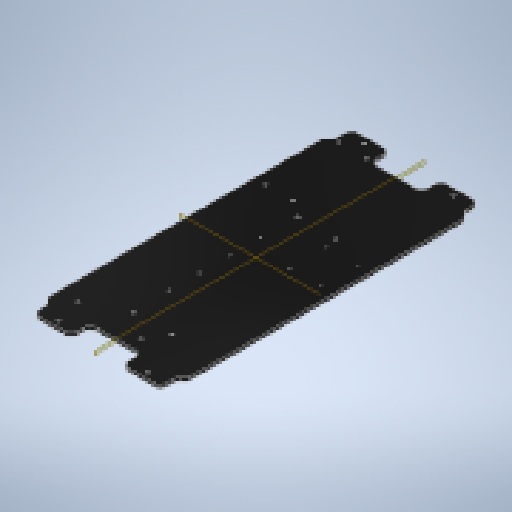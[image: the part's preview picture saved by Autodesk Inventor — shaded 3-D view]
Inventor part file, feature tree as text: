
AUTODESK INVENTOR PART (.ipt)
format: ipt  version: 2025.1 (Build 291241020, 241B)  size: 300,032 bytes
history: native  units: mm
features: sketch x10, reference x7, hole x6, other x6, extrude x4, plane x2, mirror x2, fillet x2, pattern_linear x1
ambient origin geometry x8: Origin, YZ Plane, XZ Plane, XY Plane, X Axis, Y Axis, Z Axis, Center Point
bodies: Solid1 (feature_tree)
feature tree (40):
  extrude  "Extrusion1"  Depth=220.0mm
  extrude  "Extrusion2"  Depth=5.0mm TaperAngle=0.0deg
  hole  "Hole1"  [1 undecoded]
  plane  "Work Plane1"
  plane  "Work Plane2"
  mirror  "Mirror1"
  mirror  "Mirror2"
  fillet  "Fillet1"  Radius=87.5mm
  hole  "Hole2"  [1 undecoded]
  pattern_linear  "Rectangular Pattern1"  Count1=5  [1 undecoded]
  hole  "Hole3"  [1 undecoded]
  hole  "Hole4"  [1 undecoded]
  hole  "Hole6"  [1 undecoded]
  hole  "Hole7"  [1 undecoded]
  extrude  "Extrusion4"  Depth=10.0mm
  fillet  "Fillet2"  Radius=48.0mm
  extrude  "Extrusion5"  Depth=10.0mm
  sketch  "Sketch1"  dims[d0=440.0mm d1=220.0mm]
  sketch  "Sketch2"  dims[d2=6.35mm d3=0.0mm d6=5.0mm d7=0.0mm]
  sketch  "Sketch3"  dims[d8=10.0mm]
  sketch  "Sketch4"  dims[d10=5.0mm d11=6.0mm d12=4.0mm d13=2.0mm d14=90.0deg d15=8.0mm d16=20.594885mm d17=10.0mm d18=87.5mm]
  sketch  "Sketch6"  dims[d19=132.075mm]
  sketch  "Sketch7"  dims[d20=5.0mm d21=6.0mm d22=4.0mm d23=2.0mm d24=90.0deg d25=8.0mm d26=20.594885mm d29=20.0mm d31=258.115mm d32=20.0mm d34=60.0mm]
  sketch  "Sketch9"  dims[d35=58.0mm]
  reference  "Reference4"
  reference  "Reference5"
  reference  "Reference6"
  sketch  "Sketch10"  dims[d36=49.0mm d37=50.0mm]
  reference  "Reference7"
  reference  "Reference8"
  reference  "Reference9"
  reference  "Reference10"
  sketch  "Sketch11"  dims[d38=20.0mm]
  sketch  "Sketch12"  dims[d39=2.1mm d40=6.0mm d41=4.0mm d42=2.0mm d43=90.0deg d44=6.0mm d45=0.0mm d46=100.0mm d49=5.0mm d50=6.0mm d51=10.0mm d52=2.5mm d53=90.0deg d54=8.0mm d55=20.594885mm d56=20.0mm d57=30.0mm d67=48.0mm d68=48.0mm d69=48.0mm d70=244.475mm d71=98.2375mm d72=20.0mm d73=2.6mm d74=6.0mm d75=4.0mm d76=2.0mm d77=90.0deg d78=10.0mm d79=0.0mm d80=30.0mm d81=60.0mm d82=10.0mm d83=30.0mm d84=5.0mm d85=6.0mm d86=4.0mm d87=2.0mm d88=90.0deg d89=8.0mm d90=20.594885mm d91=20.0mm d92=20.0mm d93=10.0mm d94=10.0mm d95=10.0mm d96=0.0mm d97=2.5mm d98=5.0mm d99=30.0mm d100=10.0mm d101=10.0mm d102=10.0mm d103=0.0mm]
  other  "MagDrop4.iam"
  other  "Connect4_LEG:1"
  other  "Connect4_LEG:2"
  other  "Connect4_RACK:1"
  other  "Control_Panel:1"
  other  "Control_Mount:1"
note: 7 required parameter values undecoded (feature->parameter linkage not recoverable at this tier; creation-order binding heuristic only, values carry confidence <= 0.55)
